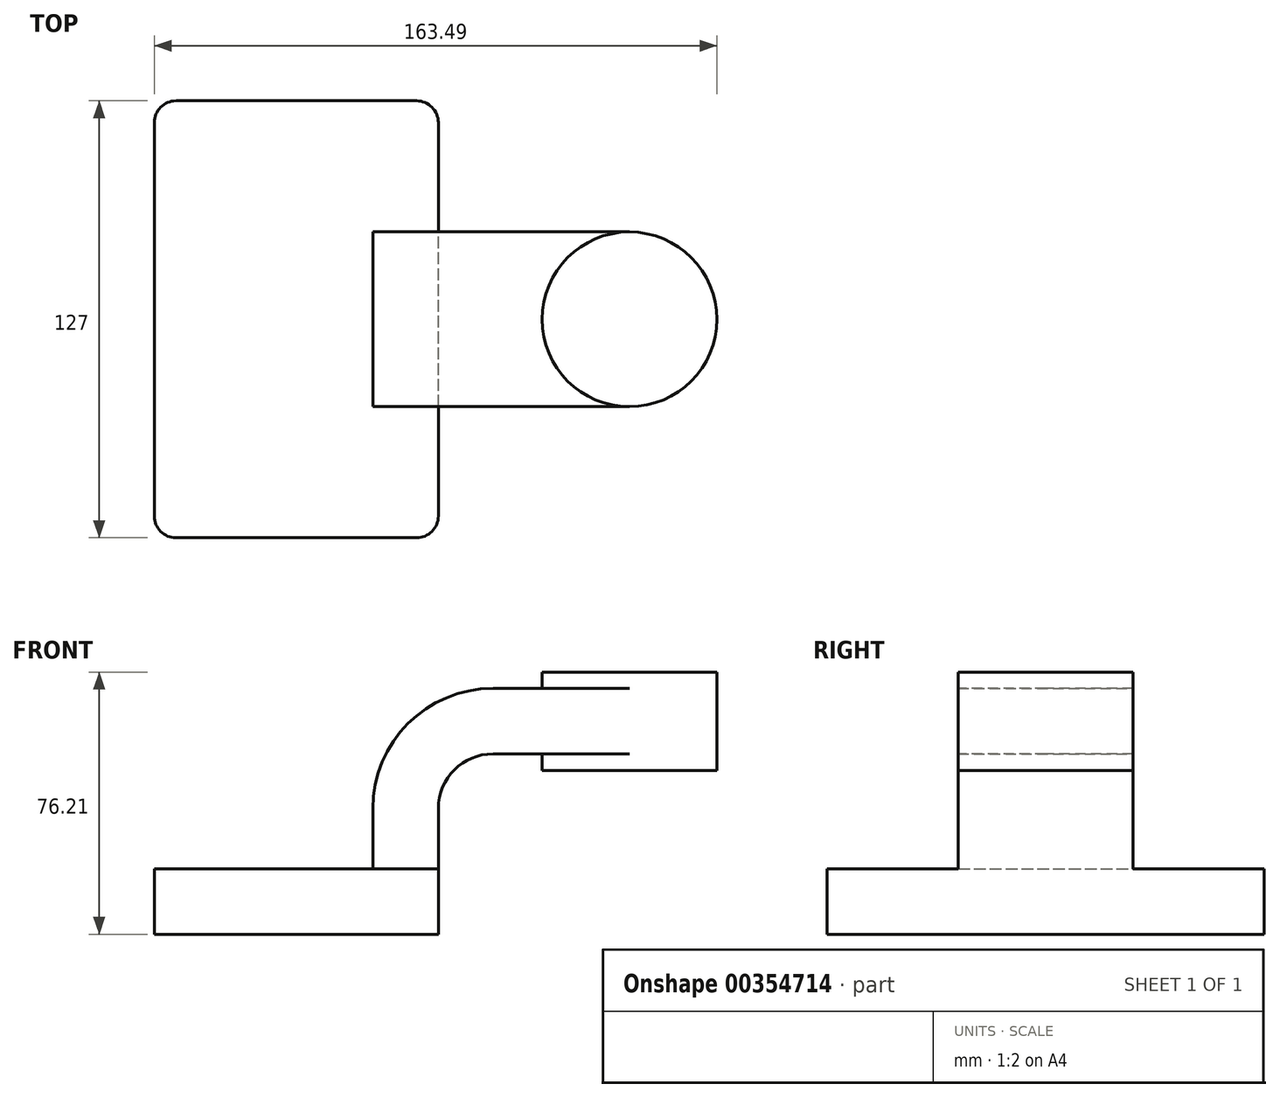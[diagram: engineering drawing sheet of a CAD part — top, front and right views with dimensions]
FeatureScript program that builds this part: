
annotation { "Feature Type Name" : "Feature", "Feature Type Description" : "" }
export const myFeature = defineFeature(function(context is Context, id is Id, definition is map)
    precondition{}
    {
        {
            var Q0;
            Q0=qCreatedBy(makeId("Front.planeOp"),FACE);
            var sketch = newSketch(context, id + "F0", { "sketchPlane" : qUnion([Q0])});
            skLineSegment(sketch, "E0.bottom", {"start": v(-41.28, -9.53) * mm, "end": v(41.28, -9.53) * mm});
            skLineSegment(sketch, "E0.top", {"start": v(-41.28, 9.53) * mm, "end": v(41.28, 9.53) * mm});
            skLineSegment(sketch, "E0.left", {"start": v(-41.28, -9.53) * mm, "end": v(-41.28, 9.53) * mm});
            skLineSegment(sketch, "E0.right", {"start": v(41.28, -9.53) * mm, "end": v(41.28, 9.53) * mm});
            skPoint(sketch, "E0.middle", {"position": v(0, 0) * mm});
            skLineSegment(sketch, "E1.bottom", {"start": v(122.22, 66.67) * mm, "end": v(71.42, 66.67) * mm});
            skLineSegment(sketch, "E1.top", {"start": v(122.22, 38.1) * mm, "end": v(71.42, 38.1) * mm});
            skLineSegment(sketch, "E1.left", {"start": v(122.22, 66.67) * mm, "end": v(122.22, 38.1) * mm});
            skLineSegment(sketch, "E1.right", {"start": v(71.42, 66.67) * mm, "end": v(71.42, 38.1) * mm});
            skPoint(sketch, "E1.middle", {"position": v(96.82, 52.39) * mm});
            skLineSegment(sketch, "E2", {"start": v(41.27, 9.52) * mm, "end": v(41.27, 27) * mm});
            skArc(sketch, "E3", {"start": v(41.27, 27) * mm, "mid": v(45.92, 38.23) * mm, "end": v(57.15, 42.88) * mm});
            skLineSegment(sketch, "E4", {"start": v(57.15, 42.88) * mm, "end": v(96.82, 42.88) * mm});
            skLineSegment(sketch, "E5.0", {"start": v(57.15, 61.93) * mm, "end": v(96.82, 61.93) * mm});
            skArc(sketch, "E5.1", {"start": v(22.22, 27) * mm, "mid": v(32.45, 51.7) * mm, "end": v(57.15, 61.93) * mm});
            skLineSegment(sketch, "E5.2", {"start": v(22.22, 9.52) * mm, "end": v(22.22, 27) * mm});
            skFitSpline(sketch, "E6", {"points": [v(-41.28, 9.53) * mm, v(57.15, 61.93) * mm], "startDerivative": vector(3.8, 97.3) * mm, "endDerivative": vector(46.57, -6.86) * mm});
            skLineSegment(sketch, "E7", {"start": v(96.82, 38.1) * mm, "end": v(96.82, 66.67) * mm});
            skSolve(sketch);
        }
        {
            var Q0;
            Q0=makeQuery(id+"F0.imprint","IMPRINT",FACE,{"disambiguationData":[TD([[makeQuery(id+"F0.imprint","IMPRINT",EDGE,{"derivedFrom":sQuery(id+"F0.wireOp",EDGE,"E0.bottom")}),1.0]])]});
            extrude(context, id + "F1", {"entities" : qUnion([Q0]), "endBound" : BoundingType.SYMMETRIC, "depth" : 127 * mm});
        }
        {
            var Q0;
            {var subQ0=sQuery(id+"F0.wireOp",EDGE,"E2");Q0=makeQuery(id+"F0.imprint","IMPRINT",FACE,{"disambiguationData":[TD([[makeQuery(id+"F0.imprint","IMPRINT",EDGE,{"derivedFrom":subQ0}),1.0]])]});}
            var Q1;
            {var subQ5=sQuery(id+"F0.wireOp",EDGE,"GdLvvSrE-QnWK-lQi8-BfTX-62G6jAuHPbrv");Q1=makeQuery(id+"F0.imprint","IMPRINT",FACE,{"disambiguationData":[TD([[makeQuery(id+"F0.imprint","IMPRINT",EDGE,{"derivedFrom":subQ5}),1.0]])]});}
            var Q2;
            {var subQ0=sQuery(id+"F0.wireOp",EDGE,"E5.0");var subQ1=sQuery(id+"F0.wireOp",EDGE,"E1.right");var subQ2=makeQuery(id+"F0.imprint","INTERSECT",VERTEX,{"derivedFrom":[subQ1,subQ0]});Q2=makeQuery(id+"F0.imprint","IMPRINT",FACE,{"disambiguationData":[TD([[makeQuery(id+"F0.imprint","IMPRINT",EDGE,{"disambiguationData":[TD([[subQ2,-1.0]])],"derivedFrom":subQ1}),1.0]])]});}
            extrude(context, id + "F2", {"entities" : qUnion([Q0, Q1, Q2]), "operationType" : NewBodyOperationType.ADD, "endBound" : BoundingType.SYMMETRIC, "depth" : 50.8 * mm});
        }
        {
            var Q0;
            Q0=makeQuery(id+"F0.imprint","IMPRINT",FACE,{"disambiguationData":[TD([[makeQuery(id+"F0.imprint","IMPRINT",EDGE,{"derivedFrom":sQuery(id+"F0.wireOp",EDGE,"E5.1")}),1.0]])]});
            extrude(context, id + "F3", {"entities" : qUnion([Q0]), "operationType" : NewBodyOperationType.ADD, "endBound" : BoundingType.SYMMETRIC, "depth" : 15.88 * mm});
        }
        {
            var Q0;
            {var subQ0=sQuery(id+"F0.wireOp",EDGE,"E1.left");Q0=makeQuery(id+"F0.imprint","IMPRINT",FACE,{"disambiguationData":[TD([[makeQuery(id+"F0.imprint","IMPRINT",EDGE,{"derivedFrom":subQ0}),-1.0]])]});}
            var Q1;
            Q1=sQuery(id+"F0.wireOp",EDGE,"E7");
            revolve(context, id + "F4", {"operationType" : NewBodyOperationType.ADD, "entities" : qUnion([Q0]), "axis" : qUnion([Q1]), "revolveType" : RevolveType.FULL});
        }
        {
            var Q0;
            Q0=makeQuery(id+"F1.opExtrude","CAP_EDGE",EDGE,{"disambiguationData":[OSD([sQuery(id+"F0.wireOp",EDGE,"E0.left")])],"isStart":false});
            var Q1;
            Q1=makeQuery(id+"F1.opExtrude","CAP_EDGE",EDGE,{"disambiguationData":[OSD([sQuery(id+"F0.wireOp",EDGE,"E0.left")])],"isStart":true});
            var Q2;
            Q2=makeQuery(id+"F1.opExtrude","CAP_EDGE",EDGE,{"disambiguationData":[OSD([sQuery(id+"F0.wireOp",EDGE,"E0.right")])],"isStart":true});
            var Q3;
            Q3=makeQuery(id+"F1.opExtrude","CAP_EDGE",EDGE,{"disambiguationData":[OSD([sQuery(id+"F0.wireOp",EDGE,"E0.right")])],"isStart":false});
            fillet(context, id + "F5", {"entities" : qUnion([Q0, Q1, Q2, Q3]), "radius" : 6.35 * mm, "tangentPropagation" : true, "allowEdgeOverflow" : false});
        }
    });
